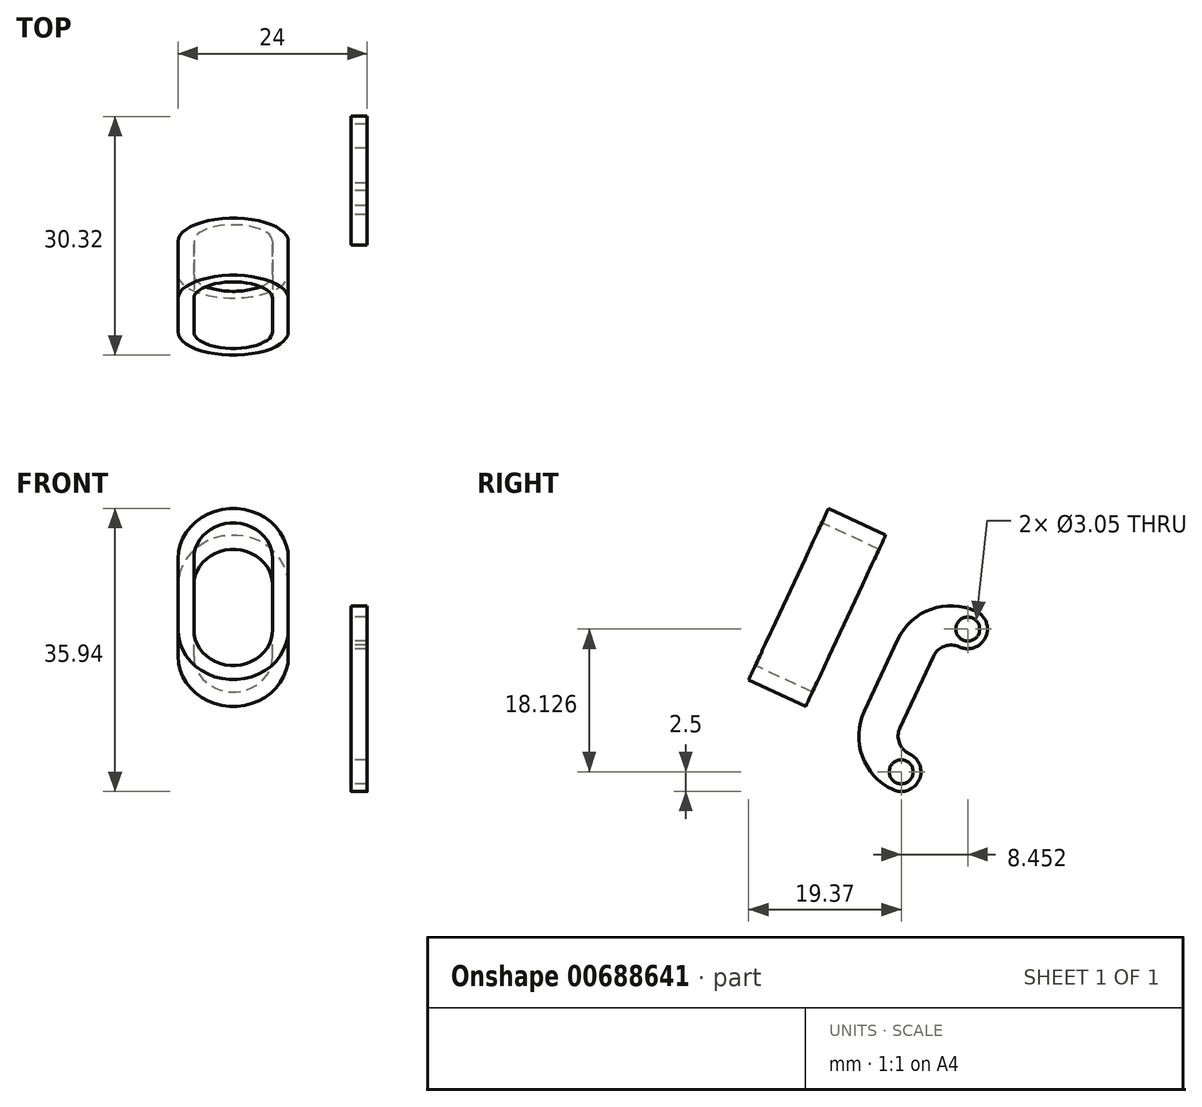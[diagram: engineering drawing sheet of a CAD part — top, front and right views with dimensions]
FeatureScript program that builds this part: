
annotation { "Feature Type Name" : "Feature", "Feature Type Description" : "" }
export const myFeature = defineFeature(function(context is Context, id is Id, definition is map)
    precondition{}
    {
        {
            var Q0;
            Q0=qCreatedBy(makeId("Right.planeOp"),FACE);
            var sketch = newSketch(context, id + "F0", { "sketchPlane" : qUnion([Q0])});
            skCircle(sketch, "E0", {"center": v(0, 0) * mm, "radius": 1.52 * mm});
            skCircle(sketch, "E1", {"center": v(8.45, 18.13) * mm, "radius": 1.52 * mm});
            skCircle(sketch, "E2", {"center": v(0, 0) * mm, "radius": 2.5 * mm});
            skCircle(sketch, "E3", {"center": v(8.45, 18.13) * mm, "radius": 2.5 * mm});
            skArc(sketch, "E4", {"start": v(7.4, 15.86) * mm, "mid": v(5.48, 15.94) * mm, "end": v(4.07, 14.65) * mm});
            skLineSegment(sketch, "E5", {"start": v(4.07, 14.65) * mm, "end": v(-0.15, 5.59) * mm});
            skLineSegment(sketch, "E6", {"start": v(0, 0) * mm, "end": v(8.45, 18.13) * mm, "construction": true});
            skArc(sketch, "E7", {"start": v(-0.15, 5.59) * mm, "mid": v(-0.24, 3.68) * mm, "end": v(1.06, 2.27) * mm});
            skLineSegment(sketch, "E8", {"start": v(-4.68, 7.7) * mm, "end": v(-0.46, 16.76) * mm});
            skArc(sketch, "E9", {"start": v(-4.68, 7.7) * mm, "mid": v(-4.93, 1.97) * mm, "end": v(-1.06, -2.27) * mm});
            skArc(sketch, "E10", {"start": v(9.5, 20.4) * mm, "mid": v(3.77, 20.64) * mm, "end": v(-0.46, 16.76) * mm});
            skSolve(sketch);
        }
        {
            var Q0;
            Q0 = qSketchRegion(id + "F0", true);
            extrude(context, id + "F1", {"entities" : qUnion([Q0]), "depth" : 2 * mm, "offsetDistance" : 25 * mm});
        }
        {
            var Q0;
            Q0=makeQuery(id+"F1.opExtrude","SWEPT_FACE",FACE,{"disambiguationData":[OSD([sQuery(id+"F0.wireOp",EDGE,"E8")])]});
            cPlane(context, id + "F2", {"entities" : qUnion([Q0]), "cplaneType" : CPlaneType.OFFSET, "offset" : 15 * mm, "width" : 150 * mm, "height" : 150 * mm});
        }
        {
            var Q0;
            Q0=qCreatedBy(id+"F2.planeOp",FACE);
            var sketch = newSketch(context, id + "F3", { "sketchPlane" : qUnion([Q0])});
            skLineSegment(sketch, "E11", {"start": v(0, 14.4) * mm, "end": v(-30, 14.4) * mm, "construction": true});
            skLineSegment(sketch, "E12", {"start": v(-15, 9.4) * mm, "end": v(-15, 19.4) * mm, "construction": true});
            skPoint(sketch, "E12.startSnap0", {"position": v(-15, 14.4) * mm});
            skArc(sketch, "E13.0.startCap", {"start": v(-10, 9.4) * mm, "mid": v(-15, 4.4) * mm, "end": v(-20, 9.4) * mm});
            skArc(sketch, "E13.0.endCap", {"start": v(-20, 19.4) * mm, "mid": v(-15, 24.4) * mm, "end": v(-10, 19.4) * mm});
            skLineSegment(sketch, "E13.0.left", {"start": v(-20, 9.4) * mm, "end": v(-20, 19.4) * mm});
            skLineSegment(sketch, "E13.0.right", {"start": v(-10, 9.4) * mm, "end": v(-10, 19.4) * mm});
            skArc(sketch, "E14.0", {"start": v(-22, 19.4) * mm, "mid": v(-15, 26.4) * mm, "end": v(-8, 19.4) * mm});
            skLineSegment(sketch, "E14.1", {"start": v(-22, 9.4) * mm, "end": v(-22, 19.4) * mm});
            skArc(sketch, "E14.2", {"start": v(-8, 9.4) * mm, "mid": v(-15, 2.4) * mm, "end": v(-22, 9.4) * mm});
            skLineSegment(sketch, "E14.3", {"start": v(-8, 9.4) * mm, "end": v(-8, 19.4) * mm});
            skSolve(sketch);
        }
        {
            var Q0;
            Q0 = qSketchRegion(id + "F3", true);
            extrude(context, id + "F4", {"entities" : qUnion([Q0]), "oppositeDirection" : true, "depth" : 8 * mm, "offsetDistance" : 25 * mm});
        }
    });
